# Revit family: lgh-n35_100rdf4(-dm)_50Hz
name_source: partatom
category: 機械設備
units: mm (PartAtom-declared; Revit-internal decimal feet)

## family parameters
OmniClass タイトル = Heat Exchangers for Ventilation Air
OmniClass 番号 = 23.75.10.34.21
パーツ タイプ = 標準
ロード時にボイドで切り取り = いいえ
丸型コネクタ寸法 = 直径を使用
作業面ベース = いいえ
共有 = いいえ
常に垂直 = はい
部屋計算ポイント = はい

## types (7) — shared parameters
Box_Depth = 116  [stored 0.380577 ft]
Box_Height = 260
Box_Width = 334
EAダクト接続口方向_変更 = いいえ
EAダクト接続口方向_通常 = はい
IfcExportAs = IfcAirToAirHeatRecoveryType
IfcExportType = ROTARYWHEEL
OAダクト接続口方向_変更 = いいえ
OAダクト接続口方向_通常 = はい
OmniClassCode = 23-27 23 19 11
URL = https://www.mitsubishielectric.co.jp
Uniclass2015Code = Pr_60_60_36_88
Uniclass2015Title = Thermal wheels
Uniclass2015Version = Systems v1.9
ドレン管径 = 32 mm
メンテナンススペース = はい
仕様書バージョン = Version1.0
企業コード = 108420
分類コード = 50052504100070
初期抵抗 = 0.0 Pa
加湿給水管径 = 23 mm
参照している仕様書等のバージョン = 公共建築物標準仕様書（機械設備工事編）平成31年度版
周波数 = 50 Hz
呼称 = 全熱交換ユニット
外気量 = 0.0 m³/h
実風量 = 0.0 m³/h
形式 = 天井埋込ダクト形
排気量 = 0.0 m³/h
本体マテリアル = 溶融亜鉛めっき鋼板
極数 = 3
法定耐用年数 = 15
消費電力_加湿器 = 0 W
点検口 = はい
点検口離隔 = 150
相 = 1
積算_科目 = 1 空気調和設備
符号 = HEU
給水管_Depth = 29  [stored 0.0951444 ft]
製品リリース年月 = 2023/3/14
製品出荷対象 = 国内
製造元 = 三菱電機株式会社
設置方法 = 天井吊(隠ぺい)形
設計風量 = 0.0 m³/h
説明 = 業務用ロスナイ 外気処理ユニット(天井埋込形加熱加湿付直膨タイプ)
負荷分類 = 3_ファン類
運転質量 = 0.00 kg
電動機出力 = 0 W
電圧 = 200 V
zero-valued in all types: Clearance Bottom, Clearance Top, 価格

## per-type parameters (varying)
- LGH-N35RDF4-DM: Box_H=23  [stored 0.0754593 ft]; Box_W=528; Clearance Left=600; Depth=1501; Duct_Change_Center=124  [stored 0.406824 ft]; Duct_Depth_OA_EA=64  [stored 0.209974 ft]; Duct_Depth_RA=70  [stored 0.229659 ft]; Duct_Depth_SA=120  [stored 0.393701 ft]; Duct_Height=111; Duct_Height_RA=136; Duct_Height_SA=203  [stored 0.66601 ft]; Duct_Pitch_OA_EA=650; Duct_Pitch_SA_RA=335; Duct_Width_SA=428; EAサイズ_D=142  [stored 0.465879 ft]; Height=331; MAX静圧=235.0 Pa; MAX風量=350.0 m³/h; MID静圧=122.0 Pa; MID風量=252.0 m³/h; MIN静圧=45.0 Pa; MIN風量=154.0 m³/h; OAサイズ_D=142  [stored 0.465879 ft]; RAサイズ_D=142  [stored 0.465879 ft]; SAサイズ_D=142  [stored 0.465879 ft]; Width=874; エンタルピ交換効率_冷房=60.00%; エンタルピ交換効率_暖房=70.00%; ドレン管_Depth=64  [stored 0.209974 ft]; ドレン管_H=292; ドレン管_W=460; 冷媒ガス管_Depth=110  [stored 0.360892 ft]; 冷媒ガス管_H=169  [stored 0.554462 ft]; 冷媒ガス管_W=306; 冷媒ガス管径=13 mm; 冷媒液管_Depth=105  [stored 0.344488 ft]; 冷媒液管_H=114  [stored 0.374016 ft]; 冷媒液管_W=358; 冷媒液管径=6 mm; 吊りボルト_高さ=85  [stored 0.278871 ft]; 吊りボルトピッチ1=922; 吊りボルトピッチ2=1493; 天吊金具_35_50=はい; 天吊金具_80_100=いいえ; 天吊金具_D=4  [stored 0.0131234 ft]; 天吊金具_幅=20  [stored 0.0656168 ft]; 天吊金具_幅2=20  [stored 0.0656168 ft]; 天吊金具_径=7  [stored 0.0229659 ft]; 有効加湿量=2.4; 機外静圧=235.0 Pa; 機外静圧_排気=235.0 Pa; 消費電力=235 W; 温度交換効率=70.50%; 点検口1_Center=444; 点検口1_Depth=450; 点検口1_Width=450; 点検口2_Depth=450; 点検口2_Width=450; 点検口高さ=-331  [stored -1.08596 ft]; 給水管_H=123  [stored 0.403543 ft]; 給水管_W=446; 製品質量=61.00 kg; 質量=73.20 kg; 面風速=5.5 m/s; 風量=350.0 m³/h; 騒音レベル(dB(A))=37
- LGH-N50RDF4: Box_H=23  [stored 0.0754593 ft]; Box_W=528; Clearance Left=600; Depth=1501; Duct_Change_Center=124  [stored 0.406824 ft]; Duct_Depth_OA_EA=79; Duct_Depth_RA=85  [stored 0.278871 ft]; Duct_Depth_SA=85  [stored 0.278871 ft]; Duct_Height=136; Duct_Height_RA=136; Duct_Height_SA=203  [stored 0.66601 ft]; Duct_Pitch_OA_EA=745; Duct_Pitch_SA_RA=446; Duct_Width_SA=428; EAサイズ_D=192  [stored 0.629921 ft]; Height=331; MAX静圧=250.0 Pa; MAX風量=500.0 m³/h; MID静圧=130.0 Pa; MID風量=360.0 m³/h; MIN静圧=48.0 Pa; MIN風量=220.0 m³/h; OAサイズ_D=192  [stored 0.629921 ft]; RAサイズ_D=192  [stored 0.629921 ft]; SAサイズ_D=192  [stored 0.629921 ft]; Width=1016; エンタルピ交換効率_冷房=64.50%; エンタルピ交換効率_暖房=73.00%; ドレン管_Depth=29  [stored 0.0951444 ft]; ドレン管_H=30  [stored 0.0984252 ft]; ドレン管_W=436; 冷媒ガス管_Depth=110  [stored 0.360892 ft]; 冷媒ガス管_H=169  [stored 0.554462 ft]; 冷媒ガス管_W=306; 冷媒ガス管径=13 mm; 冷媒液管_Depth=105  [stored 0.344488 ft]; 冷媒液管_H=114  [stored 0.374016 ft]; 冷媒液管_W=358; 冷媒液管径=6 mm; 吊りボルト_高さ=85  [stored 0.278871 ft]; 吊りボルトピッチ1=1064; 吊りボルトピッチ2=1493; 天吊金具_35_50=はい; 天吊金具_80_100=いいえ; 天吊金具_D=4  [stored 0.0131234 ft]; 天吊金具_幅=20  [stored 0.0656168 ft]; 天吊金具_幅2=20  [stored 0.0656168 ft]; 天吊金具_径=7  [stored 0.0229659 ft]; 有効加湿量=3.2; 機外静圧=250.0 Pa; 機外静圧_排気=250.0 Pa; 消費電力=300 W; 温度交換効率=74.00%; 点検口1_Center=444; 点検口1_Depth=450; 点検口1_Width=450; 点検口2_Depth=450; 点検口2_Width=450; 点検口高さ=-331  [stored -1.08596 ft]; 給水管_H=123  [stored 0.403543 ft]; 給水管_W=446; 製品質量=64.00 kg; 質量=76.80 kg; 面風速=4.4 m/s; 風量=500.0 m³/h; 騒音レベル(dB(A))=37.5
- LGH-N50RDF4-DM: Box_H=23  [stored 0.0754593 ft]; Box_W=528; Clearance Left=600; Depth=1501; Duct_Change_Center=124  [stored 0.406824 ft]; Duct_Depth_OA_EA=79; Duct_Depth_RA=85  [stored 0.278871 ft]; Duct_Depth_SA=85  [stored 0.278871 ft]; Duct_Height=136; Duct_Height_RA=136; Duct_Height_SA=203  [stored 0.66601 ft]; Duct_Pitch_OA_EA=745; Duct_Pitch_SA_RA=446; Duct_Width_SA=428; EAサイズ_D=192  [stored 0.629921 ft]; Height=331; MAX静圧=250.0 Pa; MAX風量=500.0 m³/h; MID静圧=130.0 Pa; MID風量=360.0 m³/h; MIN静圧=48.0 Pa; MIN風量=220.0 m³/h; OAサイズ_D=192  [stored 0.629921 ft]; RAサイズ_D=192  [stored 0.629921 ft]; SAサイズ_D=192  [stored 0.629921 ft]; Width=1016; エンタルピ交換効率_冷房=64.50%; エンタルピ交換効率_暖房=73.00%; ドレン管_Depth=64  [stored 0.209974 ft]; ドレン管_H=292; ドレン管_W=460; 冷媒ガス管_Depth=110  [stored 0.360892 ft]; 冷媒ガス管_H=169  [stored 0.554462 ft]; 冷媒ガス管_W=306; 冷媒ガス管径=13 mm; 冷媒液管_Depth=105  [stored 0.344488 ft]; 冷媒液管_H=114  [stored 0.374016 ft]; 冷媒液管_W=358; 冷媒液管径=6 mm; 吊りボルト_高さ=85  [stored 0.278871 ft]; 吊りボルトピッチ1=1064; 吊りボルトピッチ2=1493; 天吊金具_35_50=はい; 天吊金具_80_100=いいえ; 天吊金具_D=4  [stored 0.0131234 ft]; 天吊金具_幅=20  [stored 0.0656168 ft]; 天吊金具_幅2=20  [stored 0.0656168 ft]; 天吊金具_径=7  [stored 0.0229659 ft]; 有効加湿量=3.2; 機外静圧=250.0 Pa; 機外静圧_排気=250.0 Pa; 消費電力=300 W; 温度交換効率=74.00%; 点検口1_Center=444; 点検口1_Depth=450; 点検口1_Width=450; 点検口2_Depth=450; 点検口2_Width=450; 点検口高さ=-331  [stored -1.08596 ft]; 給水管_H=123  [stored 0.403543 ft]; 給水管_W=446; 製品質量=64.00 kg; 質量=76.80 kg; 面風速=4.4 m/s; 風量=500.0 m³/h; 騒音レベル(dB(A))=37.5
- LGH-N80RDF4: Box_H=83  [stored 0.27231 ft]; Box_W=557; Clearance Left=800; Depth=1765; Duct_Change_Center=165; Duct_Depth_OA_EA=79; Duct_Depth_RA=85  [stored 0.278871 ft]; Duct_Depth_SA=85  [stored 0.278871 ft]; Duct_Height=162  [stored 0.531496 ft]; Duct_Height_RA=199  [stored 0.652887 ft]; Duct_Height_SA=241  [stored 0.790682 ft]; Duct_Pitch_OA_EA=917; Duct_Pitch_SA_RA=735; Duct_Width_SA=323; EAサイズ_D=242  [stored 0.793963 ft]; Height=404; MAX静圧=240.0 Pa; MAX風量=800.0 m³/h; MID静圧=124.0 Pa; MID風量=576.0 m³/h; MIN静圧=46.0 Pa; MIN風量=352.0 m³/h; OAサイズ_D=242  [stored 0.793963 ft]; RAサイズ_D=242  [stored 0.793963 ft]; SAサイズ_D=242  [stored 0.793963 ft]; Width=1231; エンタルピ交換効率_冷房=63.50%; エンタルピ交換効率_暖房=72.50%; ドレン管_Depth=29  [stored 0.0951444 ft]; ドレン管_H=29  [stored 0.0951444 ft]; ドレン管_W=421; 冷媒ガス管_Depth=110  [stored 0.360892 ft]; 冷媒ガス管_H=193  [stored 0.633202 ft]; 冷媒ガス管_W=305; 冷媒ガス管径=13 mm; 冷媒液管_Depth=105  [stored 0.344488 ft]; 冷媒液管_H=138  [stored 0.452756 ft]; 冷媒液管_W=357; 冷媒液管径=6 mm; 吊りボルト_高さ=401; 吊りボルトピッチ1=1271; 吊りボルトピッチ2=1418; 天吊金具_35_50=いいえ; 天吊金具_80_100=はい; 天吊金具_D=45; 天吊金具_幅=16  [stored 0.0524934 ft]; 天吊金具_幅2=30  [stored 0.0984252 ft]; 天吊金具_径=8  [stored 0.0262467 ft]; 有効加湿量=4.8; 機外静圧=240.0 Pa; 機外静圧_排気=240.0 Pa; 消費電力=465 W; 温度交換効率=75.00%; 点検口1_Center=572; 点検口1_Depth=600; 点検口1_Width=600; 点検口2_Depth=600; 点検口2_Width=600; 点検口高さ=-404  [stored -1.32546 ft]; 給水管_H=146  [stored 0.479003 ft]; 給水管_W=445; 製品質量=97.00 kg; 質量=116.40 kg; 面風速=4.5 m/s; 風量=800.0 m³/h; 騒音レベル(dB(A))=37
- LGH-N80RDF4-DM: Box_H=83  [stored 0.27231 ft]; Box_W=557; Clearance Left=800; Depth=1765; Duct_Change_Center=165; Duct_Depth_OA_EA=79; Duct_Depth_RA=85  [stored 0.278871 ft]; Duct_Depth_SA=85  [stored 0.278871 ft]; Duct_Height=162  [stored 0.531496 ft]; Duct_Height_RA=199  [stored 0.652887 ft]; Duct_Height_SA=241  [stored 0.790682 ft]; Duct_Pitch_OA_EA=917; Duct_Pitch_SA_RA=735; Duct_Width_SA=323; EAサイズ_D=242  [stored 0.793963 ft]; Height=404; MAX静圧=240.0 Pa; MAX風量=800.0 m³/h; MID静圧=124.0 Pa; MID風量=576.0 m³/h; MIN静圧=46.0 Pa; MIN風量=352.0 m³/h; OAサイズ_D=242  [stored 0.793963 ft]; RAサイズ_D=242  [stored 0.793963 ft]; SAサイズ_D=242  [stored 0.793963 ft]; Width=1231; エンタルピ交換効率_冷房=63.50%; エンタルピ交換効率_暖房=72.50%; ドレン管_Depth=64  [stored 0.209974 ft]; ドレン管_H=292; ドレン管_W=459; 冷媒ガス管_Depth=110  [stored 0.360892 ft]; 冷媒ガス管_H=193  [stored 0.633202 ft]; 冷媒ガス管_W=305; 冷媒ガス管径=13 mm; 冷媒液管_Depth=105  [stored 0.344488 ft]; 冷媒液管_H=138  [stored 0.452756 ft]; 冷媒液管_W=357; 冷媒液管径=6 mm; 吊りボルト_高さ=401; 吊りボルトピッチ1=1271; 吊りボルトピッチ2=1418; 天吊金具_35_50=いいえ; 天吊金具_80_100=はい; 天吊金具_D=45; 天吊金具_幅=16  [stored 0.0524934 ft]; 天吊金具_幅2=30  [stored 0.0984252 ft]; 天吊金具_径=8  [stored 0.0262467 ft]; 有効加湿量=4.8; 機外静圧=240.0 Pa; 機外静圧_排気=240.0 Pa; 消費電力=465 W; 温度交換効率=75.00%; 点検口1_Center=572; 点検口1_Depth=600; 点検口1_Width=600; 点検口2_Depth=600; 点検口2_Width=600; 点検口高さ=-404  [stored -1.32546 ft]; 給水管_H=146  [stored 0.479003 ft]; 給水管_W=445; 製品質量=97.00 kg; 質量=116.40 kg; 面風速=4.5 m/s; 風量=800.0 m³/h; 騒音レベル(dB(A))=37
- LGH-N100RDF4: Box_H=83  [stored 0.27231 ft]; Box_W=557; Clearance Left=800; Depth=1765; Duct_Change_Center=165; Duct_Depth_OA_EA=79; Duct_Depth_RA=85  [stored 0.278871 ft]; Duct_Depth_SA=85  [stored 0.278871 ft]; Duct_Height=162  [stored 0.531496 ft]; Duct_Height_RA=199  [stored 0.652887 ft]; Duct_Height_SA=241  [stored 0.790682 ft]; Duct_Pitch_OA_EA=917; Duct_Pitch_SA_RA=735; Duct_Width_SA=323; EAサイズ_D=242  [stored 0.793963 ft]; Height=404; MAX静圧=235.0 Pa; MAX風量=1000.0 m³/h; MID静圧=122.0 Pa; MID風量=720.0 m³/h; MIN静圧=45.0 Pa; MIN風量=440.0 m³/h; OAサイズ_D=242  [stored 0.793963 ft]; RAサイズ_D=242  [stored 0.793963 ft]; SAサイズ_D=242  [stored 0.793963 ft]; Width=1231; エンタルピ交換効率_冷房=62.50%; エンタルピ交換効率_暖房=71.00%; ドレン管_Depth=29  [stored 0.0951444 ft]; ドレン管_H=29  [stored 0.0951444 ft]; ドレン管_W=421; 冷媒ガス管_Depth=115  [stored 0.377297 ft]; 冷媒ガス管_H=193  [stored 0.633202 ft]; 冷媒ガス管_W=305; 冷媒ガス管径=16 mm; 冷媒液管_Depth=110  [stored 0.360892 ft]; 冷媒液管_H=138  [stored 0.452756 ft]; 冷媒液管_W=357; 冷媒液管径=10 mm; 吊りボルト_高さ=401; 吊りボルトピッチ1=1271; 吊りボルトピッチ2=1418; 天吊金具_35_50=いいえ; 天吊金具_80_100=はい; 天吊金具_D=45; 天吊金具_幅=16  [stored 0.0524934 ft]; 天吊金具_幅2=30  [stored 0.0984252 ft]; 天吊金具_径=8  [stored 0.0262467 ft]; 有効加湿量=6.4; 機外静圧=235.0 Pa; 機外静圧_排気=235.0 Pa; 消費電力=655 W; 温度交換効率=71.00%; 点検口1_Center=572; 点検口1_Depth=600; 点検口1_Width=600; 点検口2_Depth=600; 点検口2_Width=600; 点検口高さ=-404  [stored -1.32546 ft]; 給水管_H=146  [stored 0.479003 ft]; 給水管_W=445; 製品質量=98.00 kg; 質量=117.60 kg; 面風速=5.7 m/s; 風量=1000.0 m³/h; 騒音レベル(dB(A))=39.5
- LGH-N100RDF4-DM: Box_H=83  [stored 0.27231 ft]; Box_W=557; Clearance Left=800; Depth=1765; Duct_Change_Center=165; Duct_Depth_OA_EA=79; Duct_Depth_RA=85  [stored 0.278871 ft]; Duct_Depth_SA=85  [stored 0.278871 ft]; Duct_Height=162  [stored 0.531496 ft]; Duct_Height_RA=199  [stored 0.652887 ft]; Duct_Height_SA=241  [stored 0.790682 ft]; Duct_Pitch_OA_EA=917; Duct_Pitch_SA_RA=735; Duct_Width_SA=323; EAサイズ_D=242  [stored 0.793963 ft]; Height=404; MAX静圧=235.0 Pa; MAX風量=1000.0 m³/h; MID静圧=122.0 Pa; MID風量=720.0 m³/h; MIN静圧=45.0 Pa; MIN風量=440.0 m³/h; OAサイズ_D=242  [stored 0.793963 ft]; RAサイズ_D=242  [stored 0.793963 ft]; SAサイズ_D=242  [stored 0.793963 ft]; Width=1231; エンタルピ交換効率_冷房=62.50%; エンタルピ交換効率_暖房=71.00%; ドレン管_Depth=64  [stored 0.209974 ft]; ドレン管_H=292; ドレン管_W=459; 冷媒ガス管_Depth=115  [stored 0.377297 ft]; 冷媒ガス管_H=193  [stored 0.633202 ft]; 冷媒ガス管_W=305; 冷媒ガス管径=16 mm; 冷媒液管_Depth=110  [stored 0.360892 ft]; 冷媒液管_H=138  [stored 0.452756 ft]; 冷媒液管_W=357; 冷媒液管径=10 mm; 吊りボルト_高さ=401; 吊りボルトピッチ1=1271; 吊りボルトピッチ2=1418; 天吊金具_35_50=いいえ; 天吊金具_80_100=はい; 天吊金具_D=45; 天吊金具_幅=16  [stored 0.0524934 ft]; 天吊金具_幅2=30  [stored 0.0984252 ft]; 天吊金具_径=8  [stored 0.0262467 ft]; 有効加湿量=6.4; 機外静圧=235.0 Pa; 機外静圧_排気=235.0 Pa; 消費電力=655 W; 温度交換効率=71.00%; 点検口1_Center=572; 点検口1_Depth=600; 点検口1_Width=600; 点検口2_Depth=600; 点検口2_Width=600; 点検口高さ=-404  [stored -1.32546 ft]; 給水管_H=146  [stored 0.479003 ft]; 給水管_W=445; 製品質量=98.00 kg; 質量=117.60 kg; 面風速=5.7 m/s; 風量=1000.0 m³/h; 騒音レベル(dB(A))=39.5

note: column(s) folded — value = type name in every type: モデル

note: [stored X ft] marks values corroborated as IEEE doubles in the binary element streams (Revit-internal decimal feet)

## geometry (parser evidence)
native form markers: Blend x6
no freeform markers — native parametric forms only
